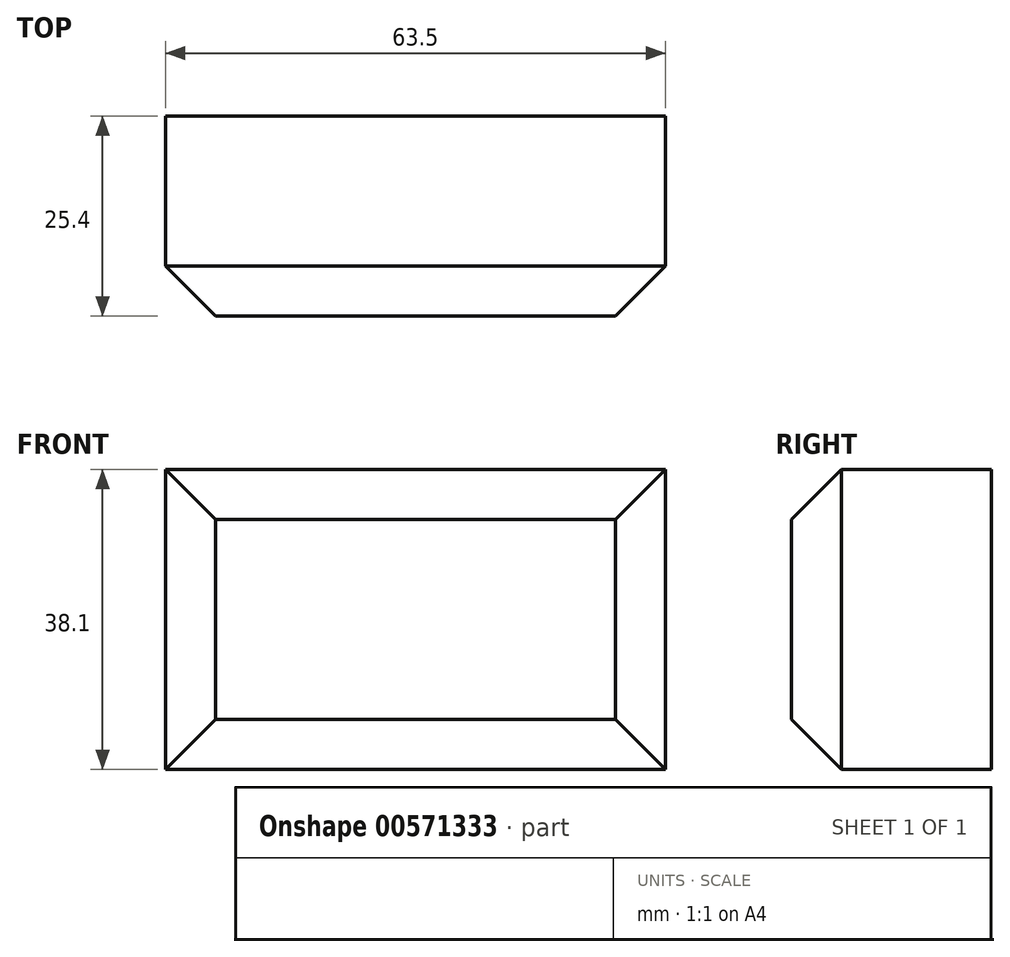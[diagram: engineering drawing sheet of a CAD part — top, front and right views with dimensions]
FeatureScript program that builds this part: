
annotation { "Feature Type Name" : "Feature", "Feature Type Description" : "" }
export const myFeature = defineFeature(function(context is Context, id is Id, definition is map)
    precondition{}
    {
        {
            var Q0;
            Q0=qCreatedBy(makeId("Front.planeOp"),FACE);
            var sketch = newSketch(context, id + "F0", { "sketchPlane" : qUnion([Q0])});
            skLineSegment(sketch, "E0.bottom", {"start": v(0, 38.1) * mm, "end": v(63.5, 38.1) * mm});
            skLineSegment(sketch, "E0.top", {"start": v(0, 0) * mm, "end": v(63.5, 0) * mm});
            skLineSegment(sketch, "E0.left", {"start": v(0, 38.1) * mm, "end": v(0, 0) * mm});
            skLineSegment(sketch, "E0.right", {"start": v(63.5, 38.1) * mm, "end": v(63.5, 0) * mm});
            skSolve(sketch);
        }
        {
            var Q0;
            Q0 = qSketchRegion(id + "F0", true);
            extrude(context, id + "F1", {"entities" : qUnion([Q0]), "depth" : 25.4 * mm, "offsetDistance" : 25.4 * mm});
        }
        {
            var Q0;
            Q0=makeQuery(id+"F1.opExtrude","CAP_EDGE",EDGE,{"disambiguationData":[OSD([sQuery(id+"F0.wireOp",EDGE,"E0.bottom")])],"isStart":false});
            var Q1;
            Q1=makeQuery(id+"F1.opExtrude","CAP_FACE",FACE,{"disambiguationData":[OSD([sQuery(id+"F0.wireOp",EDGE,"E0.bottom"),sQuery(id+"F0.wireOp",EDGE,"E0.top"),sQuery(id+"F0.wireOp",EDGE,"E0.left"),sQuery(id+"F0.wireOp",EDGE,"E0.right")])],"isStart":false});
            chamfer(context, id + "F2", {"entities" : qUnion([Q0, Q1]), "width" : 6.35 * mm, "tangentPropagation" : true});
        }
    });
